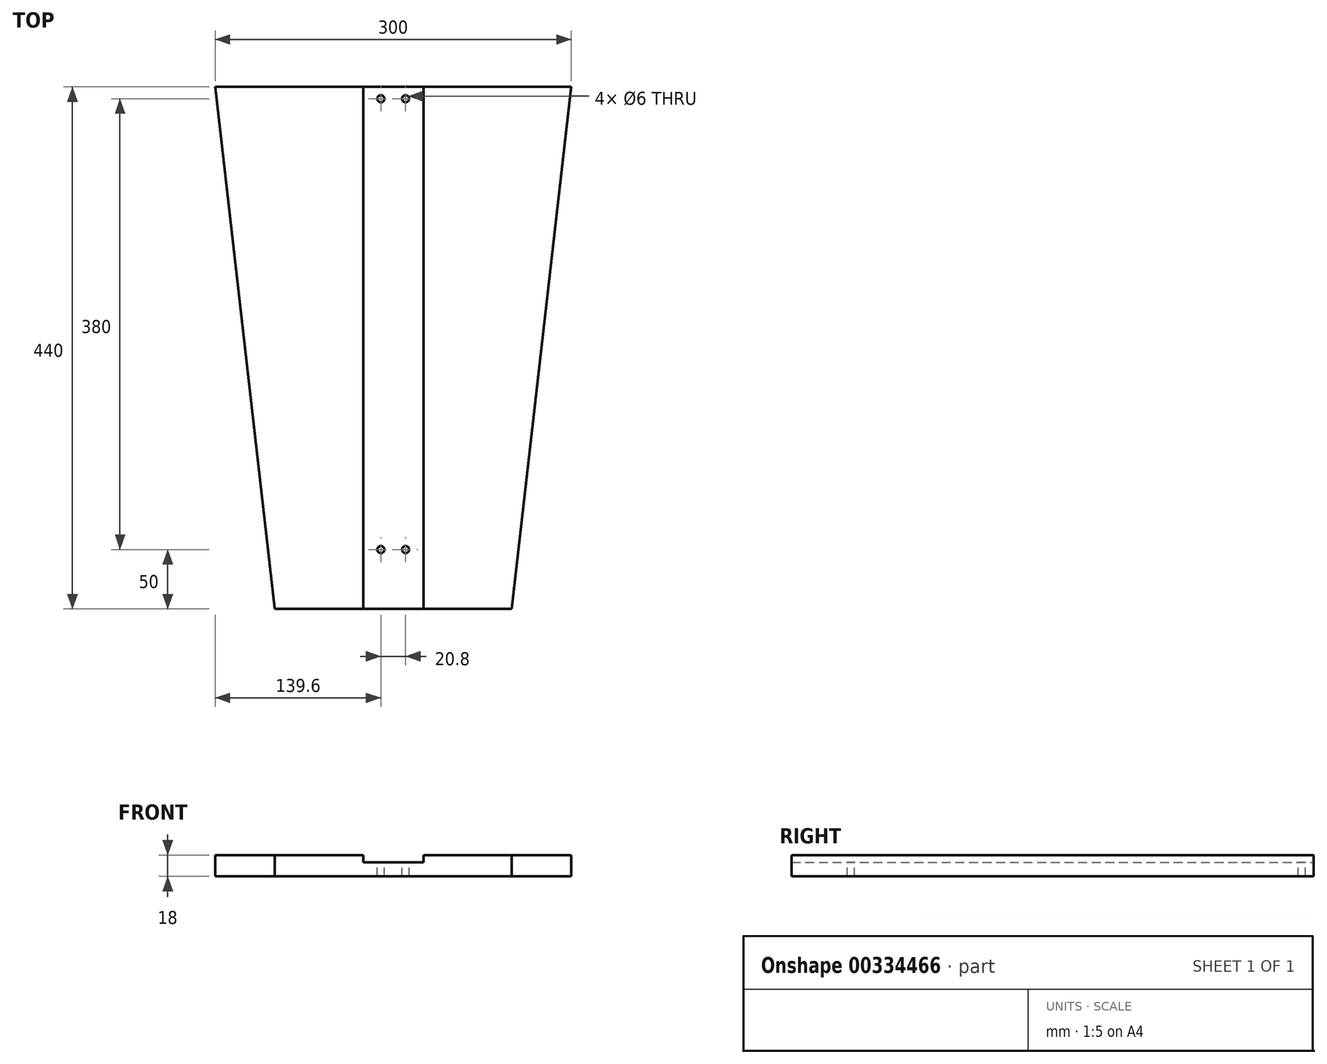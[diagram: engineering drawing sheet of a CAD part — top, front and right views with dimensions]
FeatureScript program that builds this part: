
annotation { "Feature Type Name" : "Feature", "Feature Type Description" : "" }
export const myFeature = defineFeature(function(context is Context, id is Id, definition is map)
    precondition{}
    {
        {
            var Q0;
            Q0=qCreatedBy(makeId("Top.planeOp"),FACE);
            var sketch = newSketch(context, id + "F0", { "sketchPlane" : qUnion([Q0])});
            skLineSegment(sketch, "E0.bottom", {"start": v(-400, 0) * mm, "end": v(400, 0) * mm});
            skLineSegment(sketch, "E0.top", {"start": v(-400, 440) * mm, "end": v(400, 440) * mm});
            skLineSegment(sketch, "E0.left", {"start": v(-400, 0) * mm, "end": v(-400, 440) * mm});
            skLineSegment(sketch, "E0.right", {"start": v(400, 0) * mm, "end": v(400, 440) * mm});
            skSolve(sketch);
        }
        {
            var Q0;
            Q0=makeQuery(id+"F0.imprint","IMPRINT",FACE,{"disambiguationData":[TD([[makeQuery(id+"F0.imprint","IMPRINT",EDGE,{"derivedFrom":sQuery(id+"F0.wireOp",EDGE,"E0.bottom")}),1.0]])]});
            extrude(context, id + "F1", {"entities" : qUnion([Q0]), "endBound" : BoundingType.SYMMETRIC, "depth" : 18 * mm, "offsetDistance" : 25 * mm});
        }
        {
            var Q0;
            Q0=makeQuery(id+"F1.opExtrude","CAP_FACE",FACE,{"disambiguationData":[OSD([sQuery(id+"F0.wireOp",EDGE,"E0.bottom"),sQuery(id+"F0.wireOp",EDGE,"E0.top"),sQuery(id+"F0.wireOp",EDGE,"E0.left"),sQuery(id+"F0.wireOp",EDGE,"E0.right")])],"isStart":false});
            var sketch = newSketch(context, id + "F2", { "sketchPlane" : qUnion([Q0])});
            skPoint(sketch, "E1.0.internal.orphan", {"position": v(-225.05, 0) * mm});
            skPoint(sketch, "E1.7.internal.orphan", {"position": v(0, 440) * mm});
            skLineSegment(sketch, "E2", {"start": v(-100, 0) * mm, "end": v(-150, 440) * mm});
            skLineSegment(sketch, "E3", {"start": v(100, 0) * mm, "end": v(150, 440) * mm});
            skSolve(sketch);
        }
        {
            var Q0;
            {var subQ0=sQuery(id+"F2.wireOp",EDGE,"E2");Q0=makeQuery(id+"F2.imprint","IMPRINT",FACE,{"disambiguationData":[TD([[makeQuery(id+"F2.imprint","IMPRINT",EDGE,{"derivedFrom":subQ0}),1.0]])]});}
            var Q1;
            {var subQ0=sQuery(id+"F2.wireOp",EDGE,"E3");Q1=makeQuery(id+"F2.imprint","IMPRINT",FACE,{"disambiguationData":[TD([[makeQuery(id+"F2.imprint","IMPRINT",EDGE,{"derivedFrom":subQ0}),-1.0]])]});}
            extrude(context, id + "F3", {"entities" : qUnion([Q0, Q1]), "operationType" : NewBodyOperationType.REMOVE, "oppositeDirection" : true, "depth" : 40 * mm, "offsetDistance" : 25 * mm});
        }
        {
            var Q0;
            Q0=makeQuery(id+"F1.opExtrude","CAP_FACE",FACE,{"disambiguationData":[OSD([sQuery(id+"F0.wireOp",EDGE,"E0.bottom"),sQuery(id+"F0.wireOp",EDGE,"E0.top"),sQuery(id+"F0.wireOp",EDGE,"E0.left"),sQuery(id+"F0.wireOp",EDGE,"E0.right")])],"isStart":false});
            var sketch = newSketch(context, id + "F4", { "sketchPlane" : qUnion([Q0])});
            skLineSegment(sketch, "E4.bottom", {"start": v(-25.4, 0) * mm, "end": v(25.4, 0) * mm});
            skLineSegment(sketch, "E4.top", {"start": v(-25.4, 450) * mm, "end": v(25.4, 450) * mm});
            skLineSegment(sketch, "E4.left", {"start": v(-25.4, 0) * mm, "end": v(-25.4, 450) * mm});
            skLineSegment(sketch, "E4.right", {"start": v(25.4, 0) * mm, "end": v(25.4, 450) * mm});
            skSolve(sketch);
        }
        {
            var Q0;
            Q0=makeQuery(id+"F4.imprint","IMPRINT",FACE,{"disambiguationData":[TD([[makeQuery(id+"F4.imprint","IMPRINT",EDGE,{"derivedFrom":sQuery(id+"F4.wireOp",EDGE,"E4.bottom")}),1.0]])]});
            extrude(context, id + "F5", {"entities" : qUnion([Q0]), "operationType" : NewBodyOperationType.REMOVE, "oppositeDirection" : true, "depth" : 6 * mm, "offsetDistance" : 25 * mm});
        }
        {
            var Q0;
            Q0=makeQuery(id+"F5.boolean.opBoolean","COPY",FACE,{"derivedFrom":makeQuery(id+"F5.opExtrude","CAP_FACE",FACE,{"disambiguationData":[OSD([sQuery(id+"F4.wireOp",EDGE,"E4.bottom"),sQuery(id+"F4.wireOp",EDGE,"E4.top"),sQuery(id+"F4.wireOp",EDGE,"E4.left"),sQuery(id+"F4.wireOp",EDGE,"E4.right")])],"isStart":false})});
            var sketch = newSketch(context, id + "F6", { "sketchPlane" : qUnion([Q0])});
            skLineSegment(sketch, "E5", {"start": v(-25.4, 430) * mm, "end": v(25.4, 430) * mm});
            skLineSegment(sketch, "E6", {"start": v(-10.4, 430) * mm, "end": v(-10.4, 450) * mm});
            skLineSegment(sketch, "E7", {"start": v(10.4, 430) * mm, "end": v(10.4, 450) * mm});
            skCircle(sketch, "E8", {"center": v(-10.4, 430) * mm, "radius": 3 * mm});
            skCircle(sketch, "E9", {"center": v(10.4, 430) * mm, "radius": 3 * mm});
            skLineSegment(sketch, "E10", {"start": v(-10.4, 430) * mm, "end": v(-10.4, 50) * mm});
            skLineSegment(sketch, "E11", {"start": v(-10.4, 50) * mm, "end": v(-25.4, 50) * mm});
            skLineSegment(sketch, "E12", {"start": v(-25.4, 50) * mm, "end": v(-10.4, 50) * mm});
            skLineSegment(sketch, "E13", {"start": v(-10.4, 50) * mm, "end": v(25.4, 50) * mm});
            skLineSegment(sketch, "E14", {"start": v(10.4, 50) * mm, "end": v(25.4, 50) * mm});
            skCircle(sketch, "E15", {"center": v(-10.4, 50) * mm, "radius": 3 * mm});
            skCircle(sketch, "E16", {"center": v(10.4, 50) * mm, "radius": 3 * mm});
            skSolve(sketch);
        }
        {
            var Q0;
            Q0=sQuery(id+"F6.wireOp",VERTEX,"E10.start");
            var Q1;
            Q1=sQuery(id+"F6.wireOp",VERTEX,"E7.start");
            var Q2;
            Q2=sQuery(id+"F6.wireOp",VERTEX,"E14.start");
            var Q3;
            Q3=sQuery(id+"F6.wireOp",VERTEX,"E10.end");
            var Q4;
            Q4=makeQuery(id+"F1.opExtrude","SWEPT_BODY",BODY,{"disambiguationData":[OSD([sQuery(id+"F0.wireOp",EDGE,"E0.bottom"),sQuery(id+"F0.wireOp",EDGE,"E0.top"),sQuery(id+"F0.wireOp",EDGE,"E0.left"),sQuery(id+"F0.wireOp",EDGE,"E0.right")])]});
            hole(context, id + "F7", {"style" : HoleStyle.SIMPLE, "endStyle" : HoleEndStyle.THROUGH, "holeDiameter" : 6 * mm, "isTappedThrough" : true, "tappedDepth" : 12 * mm, "tapClearance" : 3, "locations" : qUnion([Q0, Q1, Q2, Q3]), "scope" : qUnion([Q4])});
        }
    });
